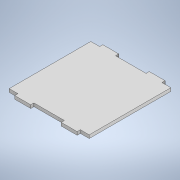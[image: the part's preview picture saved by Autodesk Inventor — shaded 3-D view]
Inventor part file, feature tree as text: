
AUTODESK INVENTOR PART (.ipt)
format: ipt  version: 2022 (Build 260153000, 153)  size: 126,464 bytes
history: native  units: mm
features: sheet_metal_op x1, sketch x1, other x1
ambient origin geometry x8: Origin, YZ Plane, XZ Plane, XY Plane, X Axis, Y Axis, Z Axis, Center Point
bodies: Solid1 (feature_tree)
feature tree (3):
  sheet_metal_op  "Face1"
  sketch  "Sketch1"  dims[d1=50.0mm d2=10.0mm d3=10.0mm d4=5.5mm d5=5.5mm d6=2.0mm d7=25.5mm d8=2.0mm]
  other  "Plate1"
